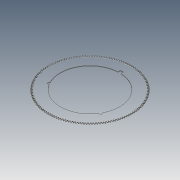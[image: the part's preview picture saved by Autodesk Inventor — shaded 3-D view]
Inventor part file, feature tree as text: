
AUTODESK INVENTOR PART (.ipt)
format: ipt  version: 2018 (Build 220112000, 112)  size: 2,771,456 bytes
history: native  units: mm
features: extrude x3, fillet x3, sketch x2, other x1, pattern_circular x1
ambient origin geometry x8: Origin, YZ Plane, XZ Plane, XY Plane, X Axis, Y Axis, Z Axis, Center Point
bodies: Solido9 (feature_tree)
feature tree (10):
  other  "<userpath>\Desktop\WaferFEM\EVOLUZ_test2.xlsx"
  extrude  "Estrusione28"  Depth=89.999444mm
  extrude  "Estrusione31"  Depth=0.316356mm
  fillet  "Raccordo15"  Radius=88.862965mm
  fillet  "Raccordo16"  Radius=0.756489mm
  fillet  "Raccordo17"  Radius=87.724869mm
  pattern_circular  "Serie circolare9"  [2 undecoded]
  extrude  "Estrusione32"  Depth=86.585838mm
  sketch  "Schizzo44"
  sketch  "Schizzo45"
note: 2 required parameter values undecoded (feature->parameter linkage not recoverable at this tier; creation-order binding heuristic only, values carry confidence <= 0.55)
